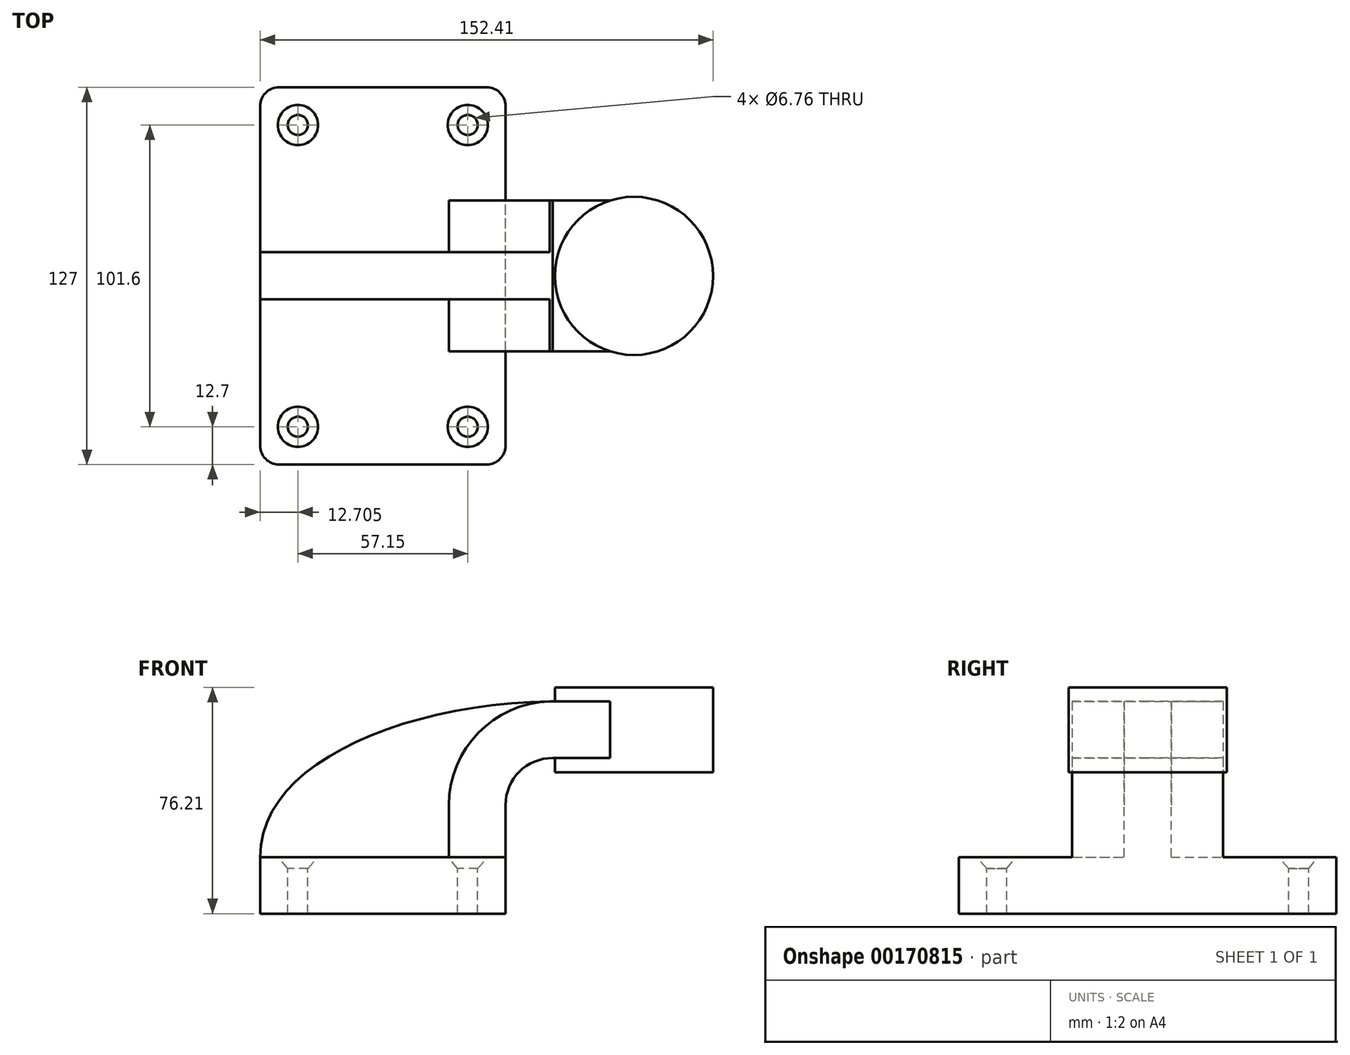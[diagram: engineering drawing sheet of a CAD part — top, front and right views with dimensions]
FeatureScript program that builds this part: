
annotation { "Feature Type Name" : "Feature", "Feature Type Description" : "" }
export const myFeature = defineFeature(function(context is Context, id is Id, definition is map)
    precondition{}
    {
        {
            var Q0;
            Q0=qCreatedBy(makeId("Front.planeOp"),FACE);
            var sketch = newSketch(context, id + "F0", { "sketchPlane" : qUnion([Q0])});
            skLineSegment(sketch, "E0.bottom", {"start": v(-41.28, 9.52) * mm, "end": v(41.27, 9.53) * mm});
            skLineSegment(sketch, "E0.top", {"start": v(-41.28, -9.53) * mm, "end": v(41.28, -9.53) * mm});
            skLineSegment(sketch, "E0.left", {"start": v(-41.28, 9.52) * mm, "end": v(-41.27, -9.53) * mm});
            skLineSegment(sketch, "E0.right", {"start": v(41.28, 9.53) * mm, "end": v(41.28, -9.52) * mm});
            skPoint(sketch, "E0.middle", {"position": v(0, 0) * mm});
            skLineSegment(sketch, "E1.bottom", {"start": v(111.12, 38.1) * mm, "end": v(60.32, 38.1) * mm});
            skLineSegment(sketch, "E1.top", {"start": v(111.12, 66.67) * mm, "end": v(60.32, 66.67) * mm});
            skLineSegment(sketch, "E1.left", {"start": v(111.12, 38.1) * mm, "end": v(111.12, 66.68) * mm});
            skLineSegment(sketch, "E1.right", {"start": v(60.32, 38.1) * mm, "end": v(60.32, 66.68) * mm});
            skPoint(sketch, "E1.middle", {"position": v(85.72, 52.39) * mm});
            skLineSegment(sketch, "E2", {"start": v(41.27, 9.53) * mm, "end": v(41.27, 27) * mm});
            skArc(sketch, "E3", {"start": v(41.27, 27) * mm, "mid": v(45.92, 38.23) * mm, "end": v(57.15, 42.88) * mm});
            skLineSegment(sketch, "E4", {"start": v(57.15, 42.88) * mm, "end": v(84.5, 42.88) * mm});
            skLineSegment(sketch, "E5.0", {"start": v(57.15, 61.93) * mm, "end": v(84.5, 61.93) * mm});
            skArc(sketch, "E5.1", {"start": v(22.23, 27) * mm, "mid": v(32.45, 51.7) * mm, "end": v(57.15, 61.93) * mm});
            skLineSegment(sketch, "E5.2", {"start": v(22.22, 9.53) * mm, "end": v(22.22, 27) * mm});
            skLineSegment(sketch, "E6", {"start": v(84.5, 38.1) * mm, "end": v(84.5, 66.67) * mm});
            skPoint(sketch, "E6.startSnap0", {"position": v(85.72, 38.1) * mm});
            skFitSpline(sketch, "E7", {"points": [v(-41.28, 9.53) * mm, v(57.15, 61.93) * mm], "startDerivative": vector(-0.82, 94.79) * mm, "endDerivative": vector(150.12, 1.74) * mm});
            skSolve(sketch);
        }
        {
            var Q0;
            Q0=makeQuery(id+"F0.imprint","IMPRINT",FACE,{"disambiguationData":[TD([[makeQuery(id+"F0.imprint","IMPRINT",EDGE,{"derivedFrom":sQuery(id+"F0.wireOp",EDGE,"E0.top")}),1.0]])]});
            extrude(context, id + "F1", {"entities" : qUnion([Q0]), "endBound" : BoundingType.SYMMETRIC, "depth" : 127 * mm});
        }
        {
            var Q0;
            {var subQ1=sQuery(id+"F0.wireOp",EDGE,"E2");Q0=makeQuery(id+"F0.imprint","IMPRINT",FACE,{"disambiguationData":[TD([[makeQuery(id+"F0.imprint","IMPRINT",EDGE,{"derivedFrom":subQ1}),1.0]])]});}
            var Q1;
            {var subQ0=sQuery(id+"F0.wireOp",EDGE,"E4");var subQ1=sQuery(id+"F0.wireOp",EDGE,"E1.right");var subQ2=makeQuery(id+"F0.imprint","INTERSECT",VERTEX,{"derivedFrom":[subQ1,subQ0]});Q1=makeQuery(id+"F0.imprint","IMPRINT",FACE,{"disambiguationData":[TD([[makeQuery(id+"F0.imprint","IMPRINT",EDGE,{"disambiguationData":[TD([[subQ2,-1.0]])],"derivedFrom":subQ1}),-1.0]])]});}
            extrude(context, id + "F2", {"entities" : qUnion([Q0, Q1]), "operationType" : NewBodyOperationType.ADD, "endBound" : BoundingType.SYMMETRIC, "depth" : 50.8 * mm});
        }
        {
            var Q0;
            {var subQ3=sQuery(id+"F0.wireOp",EDGE,"E5.2");Q0=makeQuery(id+"F0.imprint","IMPRINT",FACE,{"disambiguationData":[TD([[makeQuery(id+"F0.imprint","IMPRINT",EDGE,{"derivedFrom":subQ3}),1.0]])]});}
            extrude(context, id + "F3", {"entities" : qUnion([Q0]), "operationType" : NewBodyOperationType.ADD, "endBound" : BoundingType.SYMMETRIC, "depth" : 15.88 * mm});
        }
        {
            var Q0;
            {var subQ0=sQuery(id+"F0.wireOp",EDGE,"E1.left");Q0=makeQuery(id+"F0.imprint","IMPRINT",FACE,{"disambiguationData":[TD([[makeQuery(id+"F0.imprint","IMPRINT",EDGE,{"derivedFrom":subQ0}),1.0]])]});}
            var Q1;
            Q1=sQuery(id+"F0.wireOp",EDGE,"E6");
            revolve(context, id + "F4", {"operationType" : NewBodyOperationType.ADD, "entities" : qUnion([Q0]), "axis" : qUnion([Q1]), "revolveType" : RevolveType.FULL});
        }
        {
            var Q0;
            Q0=makeQuery(id+"F1.opExtrude","CAP_EDGE",EDGE,{"disambiguationData":[OSD([sQuery(id+"F0.wireOp",EDGE,"E0.left")])],"isStart":false});
            var Q1;
            Q1=makeQuery(id+"F1.opExtrude","CAP_EDGE",EDGE,{"disambiguationData":[OSD([sQuery(id+"F0.wireOp",EDGE,"E0.right")])],"isStart":false});
            var Q2;
            Q2=makeQuery(id+"F1.opExtrude","CAP_EDGE",EDGE,{"disambiguationData":[OSD([sQuery(id+"F0.wireOp",EDGE,"E0.left")])],"isStart":true});
            var Q3;
            Q3=makeQuery(id+"F1.opExtrude","CAP_EDGE",EDGE,{"disambiguationData":[OSD([sQuery(id+"F0.wireOp",EDGE,"E0.right")])],"isStart":true});
            fillet(context, id + "F5", {"entities" : qUnion([Q0, Q1, Q2, Q3]), "radius" : 6.35 * mm, "tangentPropagation" : true, "allowEdgeOverflow" : false});
        }
        {
            var Q0;
            {var subQ4=sQuery(id+"F0.wireOp",EDGE,"E0.bottom");var subQ5=sQuery(id+"F0.wireOp",EDGE,"E0.right");var subQ6=sQuery(id+"F0.wireOp",EDGE,"E0.left");Q0=makeQuery(id+"F3.boolean.opBoolean","SPLIT",FACE,{"disambiguationData":[TD([makeQuery(id+"F1.opExtrude","CAP_FACE",FACE,{"disambiguationData":[OSD([subQ4,sQuery(id+"F0.wireOp",EDGE,"E0.top"),subQ6,subQ5])],"isStart":true})])],"derivedFrom":makeQuery(id+"F1.opExtrude","SWEPT_FACE",FACE,{"disambiguationData":[OSD([subQ4])]})});}
            var sketch = newSketch(context, id + "F6", { "sketchPlane" : qUnion([Q0])});
            skCircle(sketch, "E8", {"center": v(-28.57, 50.8) * mm, "radius": 3.17 * mm});
            skCircle(sketch, "E9.0.1.0", {"center": v(-28.57, -50.8) * mm, "radius": 3.17 * mm});
            skCircle(sketch, "E9.1.0.0", {"center": v(28.58, 50.8) * mm, "radius": 3.17 * mm});
            skCircle(sketch, "E9.1.1.0", {"center": v(28.58, -50.8) * mm, "radius": 3.17 * mm});
            skLineSegment(sketch, "E9.direction1", {"start": v(-28.57, 50.8) * mm, "end": v(28.58, 50.8) * mm, "construction": true});
            skLineSegment(sketch, "E9.direction2", {"start": v(-28.57, 50.8) * mm, "end": v(-28.57, -50.8) * mm, "construction": true});
            skSolve(sketch);
        }
        {
            var Q0;
            Q0=sQuery(id+"F6.wireOp",VERTEX,"E8.center");
            var Q1;
            Q1=sQuery(id+"F6.wireOp",VERTEX,"E9.1.0.0.center");
            var Q2;
            Q2=sQuery(id+"F6.wireOp",VERTEX,"E9.0.1.0.center");
            var Q3;
            Q3=sQuery(id+"F6.wireOp",VERTEX,"E9.1.1.0.center");
            var Q4;
            Q4=makeQuery(id+"F1.opExtrude","SWEPT_BODY",BODY,{"disambiguationData":[OSD([sQuery(id+"F0.wireOp",EDGE,"E0.bottom"),sQuery(id+"F0.wireOp",EDGE,"E0.top"),sQuery(id+"F0.wireOp",EDGE,"E0.left"),sQuery(id+"F0.wireOp",EDGE,"E0.right")])]});
            hole(context, id + "F7", {"style" : HoleStyle.C_SINK, "endStyle" : HoleEndStyle.THROUGH, "standardTappedOrClearance" : lookupTablePath({ "standard" : "ANSI", "fit" : "Normal (ASME)", "size" : "1/4", "type" : "Clearance" }), "standardBlindInLast" : lookupTablePath({ "fit" : "Free", "standard" : "ANSI", "size" : "1/4", "type" : "Clearance" }), "holeDiameter" : 6.76 * mm, "cSinkDiameter" : 13.5 * mm, "cSinkAngle" : 82 * degree, "locations" : qUnion([Q0, Q1, Q2, Q3]), "scope" : qUnion([Q4]), "isTappedThrough" : true});
        }
    });
